FCSTD DOCUMENT  (FreeCAD 0.15R4671 (Git))
Label: Kartensortiermaschine_Sketch1
License: All rights reserved
LicenseURL: http://en.wikipedia.org/wiki/All_rights_reserved
objects: Part::Box×14, Part::Cut×11, Part::Cylinder×2, Part::Torus×1
note: 28 computed .brp shape members not serialized (recipe doc carries the construction recipe); baked Part::Feature solids carry a one-line shape summary decoded from their .brp

FEATURE [Part::Torus] Torus
  Angle1 = -180
  Angle2 = 180
  Angle3 = 360
  Radius1 = 610
  Radius2 = 100
FEATURE [Part::Box] Box  label="Würfel"
  Height = 150
  Length = 1500
  Placement = pos=(-750,-750,0) rot=(0,0,1;0rad)
  Width = 1500
FEATURE [Part::Cut] Cut
  Base = -> Torus
  Tool = -> Box
FEATURE [Part::Cylinder] Cylinder  label="Zylinder"
  Angle = 360
  Height = 300
  Placement = pos=(0,0,-200) rot=(0,0,1;0rad)
  Radius = 110
FEATURE [Part::Box] Box001  label="Würfel001"
  Height = 50
  Length = 100
  Placement = pos=(12,-60,0) rot=(0,0,1;0rad)
  Width = 120
FEATURE [Part::Box] Box003  label="Würfel003"
  Height = 30
  Length = 120
  Placement = pos=(4,-55,10) rot=(0,0,1;0rad)
  Width = 110
FEATURE [Part::Box] Box004  label="Würfel004"
  Height = 30
  Length = 120
  Placement = pos=(4,-55,10) rot=(0,0,1;0rad)
  Width = 110
FEATURE [Part::Cut] Cut003
  Base = -> Box001
  Tool = -> Box004
FEATURE [Part::Box] Box007  label="Würfel005"
  Height = 10
  Length = 380
  Placement = pos=(126,-50,0) rot=(0,0,1;0rad)
  Width = 100
FEATURE [Part::Cylinder] Cylinder001  label="Zylinder001"
  Angle = 360
  Height = 300
  Placement = pos=(0,0,-10) rot=(0,0,1;0rad)
  Radius = 100
FEATURE [Part::Cut] Cut004
  Base = -> Cylinder
  Tool = -> Cylinder001
FEATURE [Part::Box] Box008  label="Würfel006"
  Height = 30
  Length = 120
  Placement = pos=(4,-55,10) rot=(0,0,1;0rad)
  Width = 110
FEATURE [Part::Cut] Cut005
  Base = -> Cut004
  Tool = -> Box008
FEATURE [Part::Cut] Cut006
  Base = -> Cut003
  Tool = -> Box003
FEATURE [Part::Box] Box009  label="Würfel007"
  Height = 10
  Length = 100
  Placement = pos=(100,-25,0) rot=(0,0,1;0rad)
  Width = 50
FEATURE [Part::Box] Box010  label="Würfel008"
  Height = 10
  Length = 100
  Placement = pos=(100,-25,0) rot=(0,0,1;0rad)
  Width = 50
FEATURE [Part::Cut] Cut007
  Base = -> Box007
  Tool = -> Box010
FEATURE [Part::Cut] Cut008
  Base = -> Cut006
  Tool = -> Box009
FEATURE [Part::Box] Box011  label="Würfel009"
  Height = 10
  Length = 250
  Placement = pos=(245,-25,0) rot=(0,0,1;0rad)
  Width = 50
FEATURE [Part::Cut] Cut009
  Base = -> Cut007
  Tool = -> Box011
FEATURE [Part::Box] Box012  label="Würfel010"
  Height = 10
  Length = 250
  Placement = pos=(90,-50,-85) rot=(0,-1,0;0.349066rad)
  Width = 100
FEATURE [Part::Box] Box013  label="Würfel011"
  Height = 10
  Length = 100
  Placement = pos=(260,-25,0) rot=(0,0,1;0rad)
  Width = 50
FEATURE [Part::Cut] Cut010
  Base = -> Box012
  Tool = -> Box013
FEATURE [Part::Box] Box014  label="Würfel012"
  Height = 10
  Length = 380
  Placement = pos=(126,-50,0) rot=(0,0,1;0rad)
  Width = 100
FEATURE [Part::Box] Box015  label="Würfel013"
  Height = 10
  Length = 100
  Placement = pos=(100,-25,0) rot=(0,0,1;0rad)
  Width = 50
FEATURE [Part::Cut] Cut011
  Base = -> Box014
  Tool = -> Box015
FEATURE [Part::Box] Box016  label="Würfel014"
  Height = 10
  Length = 250
  Placement = pos=(245,-25,0) rot=(0,0,1;0rad)
  Width = 50
FEATURE [Part::Cut] Cut012
  Base = -> Cut011
  Placement = pos=(100000,0,0) rot=(0,0,1;0rad)
  Tool = -> Box016
